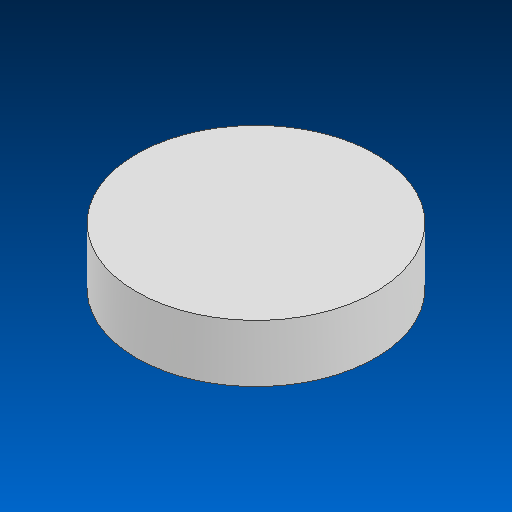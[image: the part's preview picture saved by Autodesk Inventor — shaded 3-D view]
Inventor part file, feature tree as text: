
AUTODESK INVENTOR PART (.ipt)
format: ipt  version: 2022.2 (Build 262287000, 287)  size: 83,456 bytes
history: native  units: in
note: dims shown in document units (in); Inventor stores cm internally (conversion verified against a paired STEP export)
features: revolve x1
ambient origin geometry x8: Origin, YZ Plane, XZ Plane, XY Plane, X Axis, Y Axis, Z Axis, Center Point
bodies: Solid1 (feature_tree)
feature tree (1):
  revolve  "Revolve1"  [1 undecoded]
note: 1 required parameter value undecoded (feature->parameter linkage not recoverable at this tier; creation-order binding heuristic only, values carry confidence <= 0.55)
